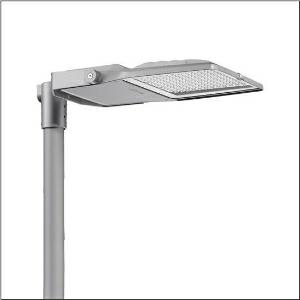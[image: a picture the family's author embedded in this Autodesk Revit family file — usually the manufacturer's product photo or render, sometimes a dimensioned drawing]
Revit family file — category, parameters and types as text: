
# Revit family: floodlight_fl_21_midi___pl52_5xa7781e2d3a_9309
name_source: partatom
category: Lighting Fixtures
units: mm (PartAtom-declared; Revit-internal decimal feet)

## family parameters
Cut with Voids When Loaded = No
Host = Face
Light Source = No
Part Type = Normal
Room Calculation Point = No
Round Connector Dimension = Use Diameter
Shared = No

## types (1)
- --- (1 x LED, 26850 lm, 208.1 W, 3000K)
    Apparent Load = 208 VA
    CIE Flux Codes = 26 60 98 100 100
    Color Rendering = 70
    Color Temperature = 3000K
    Default Elevation = 1800 mm
    Description = Floodlight FL 21 midi, floodlight, primary light control with lens, of PMMA, primary optical cover: protective disc, of toughened safety glass, transparent, light distribution: PL52, light emission: direct distribution, installation type: surface-mounted, LED, High Power LED, rated luminous flux: 26.850lm, luminous efficacy: 129lm/W, light colour: 730, colour temperature: 3000K, control gear: ECG iQ, control: optimised constant luminous flux control (CLO 2.0), Desk-Remote (wireless, voltage-free reading and setting of iQ features in the workshop via application-optimized NFC function/RFID function), Light-Fading, Smart-Wire, Night-Set, Lumen-Switch, Temp-Guard, Auto-Match, with terminal, 6-pole, mains connection: 220..240V, AC, 50/60Hz, start of lifetime: 208W, end of lifetime: 227W, reduction: 90W, luminaire housing, of diecast aluminium, powder-coated, Siteco® metallic grey (DB 702S), corrosivity category C5 according to DIN EN ISO 12944, mast bracket, of steel, galvanised, powder-coated, Siteco® metallic grey (DB 702S), protection rating (complete): IP66, insulation class (complete): insulation class I (protective earthing), certification: CE, protection symbol: D, impact resistance: IK08, permissible operating ambient temperature: -40..+40°C, permissible operating ambient temperature for outdoor applications: -40..+50°C, standard: DIN EN 12944, packaging unit: 1 piece

Light Distribution: PL52
    Height = 76 mm
    Lamp = 1 x LED
    Lamp Light Flux = 26850 lm
    Lamp Power = 208.1 W
    Lamp count = 1
    Length = 657 mm
    Luminous efficacy = 129 lm/W
    Manufacturer = Siteco
    ModVariant = No
    Model = 5XA7781E2D3A
    Number of Poles = 1
    OnlyDefault = Yes
    Power Factor = 1
    Product Name = Floodlight FL 21 midi | PL52
    Product group = floodlight | pylon top
    ProductGroupID = 6101
    Protection Class = Protection class I
    Protection Degree = IP 66
    RLX_Detail_Level = 1
    RlxData = <blob elided: 153745 chars, md5=8720a85a>
    Socket = socket
    Standby Power = 0 W
    System Light Flux = 26850 lm
    System Power = 208 W
    Type Comments = factory setting: luminous flux: 100 % | dim-lin: 254 | 710 mA
    Type Image = l_1007123.jpg
    URL = http://relux.com
    VarID = @adj_014881
    Voltage = 0 V
    Weight = 0.00 kg
    Width = 442 mm

## geometry (parser evidence)
native form markers: Blend x4, Sweep x11
no freeform markers — native parametric forms only
